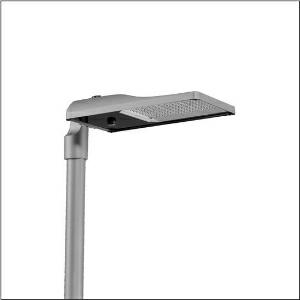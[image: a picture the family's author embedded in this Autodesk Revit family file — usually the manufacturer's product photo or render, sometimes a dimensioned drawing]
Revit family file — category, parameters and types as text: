
# Revit family: streetlight_sl_31_maxi___st0_5a_5xh8b31t08ta_8beb
name_source: partatom
category: Lighting Fixtures
units: mm (PartAtom-declared; Revit-internal decimal feet)

## family parameters
Cut with Voids When Loaded = No
Host = Face
Light Source = No
Part Type = Normal
Room Calculation Point = No
Round Connector Dimension = Use Diameter
Shared = No

## types (1)
- --- (1 x LED, 33650 lm, 228.8 W, 3000K)
    Apparent Load = 229 VA
    CIE Flux Codes = 43 76 97 100 100
    Color Rendering = 70
    Color Temperature = 3000K
    Default Elevation = 1800 mm
    Description = Streetlight SL 31 maxi D4i, Desk-Remote mast luminaire for post-top, side-entry; light control with lens of PMMA; light distribution: ST0.5a, direct asymmetric distribution, for standard-compliant lighting for roads and squares; LED: luminous flux: 33.650lm, light colour: 730, colour temperature: 3000K; luminous efficacy: 147,1lm/W; control: pre-setting: logarithmic dimming characteristic, flexible luminous flux parameterisation, time-dependent luminous flux control, constant luminous flux control, power reduction, intelligent temperature release in ECG and LED module, overheat protection; luminaire housing, of diecast aluminium, SITECO metallic grey (DB 702S), corrosivity category C5 high according to DIN EN ISO 12944; cover of toughened safety glass, transparent, opened without tools; mast flange of diecast aluminium, SITECO metallic grey (DB 702S), spigot size: 76/60mm, mast flange included unmounted; cable length: 14,5m, connection cable pre-assembled; mains connection: 220..240V, AC, 50/60Hz; power consumption (at start of service life): 228,8W / (at end of service life): 248,7W / (with reduced operation 50%): 102,4W; protection rating (complete): IP66; insulation class (complete): insulation class II (safety insulation); impact resistance: IK09; certification: CE, ENEC, ENEC+, VDE, UKCA, ZD4i; permissible operating ambient temperature for outdoor applications: -40..+50°C; packaging unit: 1 piece

Light Distribution: ST0.5a
    Height = 79 mm
    Lamp = 1 x LED
    Lamp Light Flux = 33650 lm
    Lamp Power = 228.8 W
    Lamp count = 1
    Length = 657 mm
    Luminous efficacy = 147 lm/W
    Manufacturer = Siteco
    ModVariant = No
    Model = 5XH8B31T08TA
    Number of Poles = 1
    OnlyDefault = Yes
    Power Factor = 1
    Product Name = Streetlight SL 31 maxi | ST0.5a
    Product group = mast luminaire | pylon top
    ProductGroupID = 6100
    Protection Class = Protection class II
    Protection Degree = IP 66
    RLX_Detail_Level = 1
    RLX_Emergency_Light_Flux = 0 lm
    RLX_Emergency_Type = 0
    RLX_Emergency_Type_DB = No
    RlxData = <blob elided: 58529 chars, md5=ab4a4147>
    Socket = socket
    Standby Power = 0 W
    System Light Flux = 33650 lm
    System Power = 229 W
    Type Comments = factory setting: luminous flux: 100 % | dim-lin: 254 | 802 mA
    Type Image = l_1300303.jpg
    URL = http://relux.com
    VarID = @adj_046939
    Voltage = 0 V
    Weight = 0.00 kg
    Width = 362 mm

## geometry (parser evidence)
native form markers: Blend x4, Sweep x11
no freeform markers — native parametric forms only
